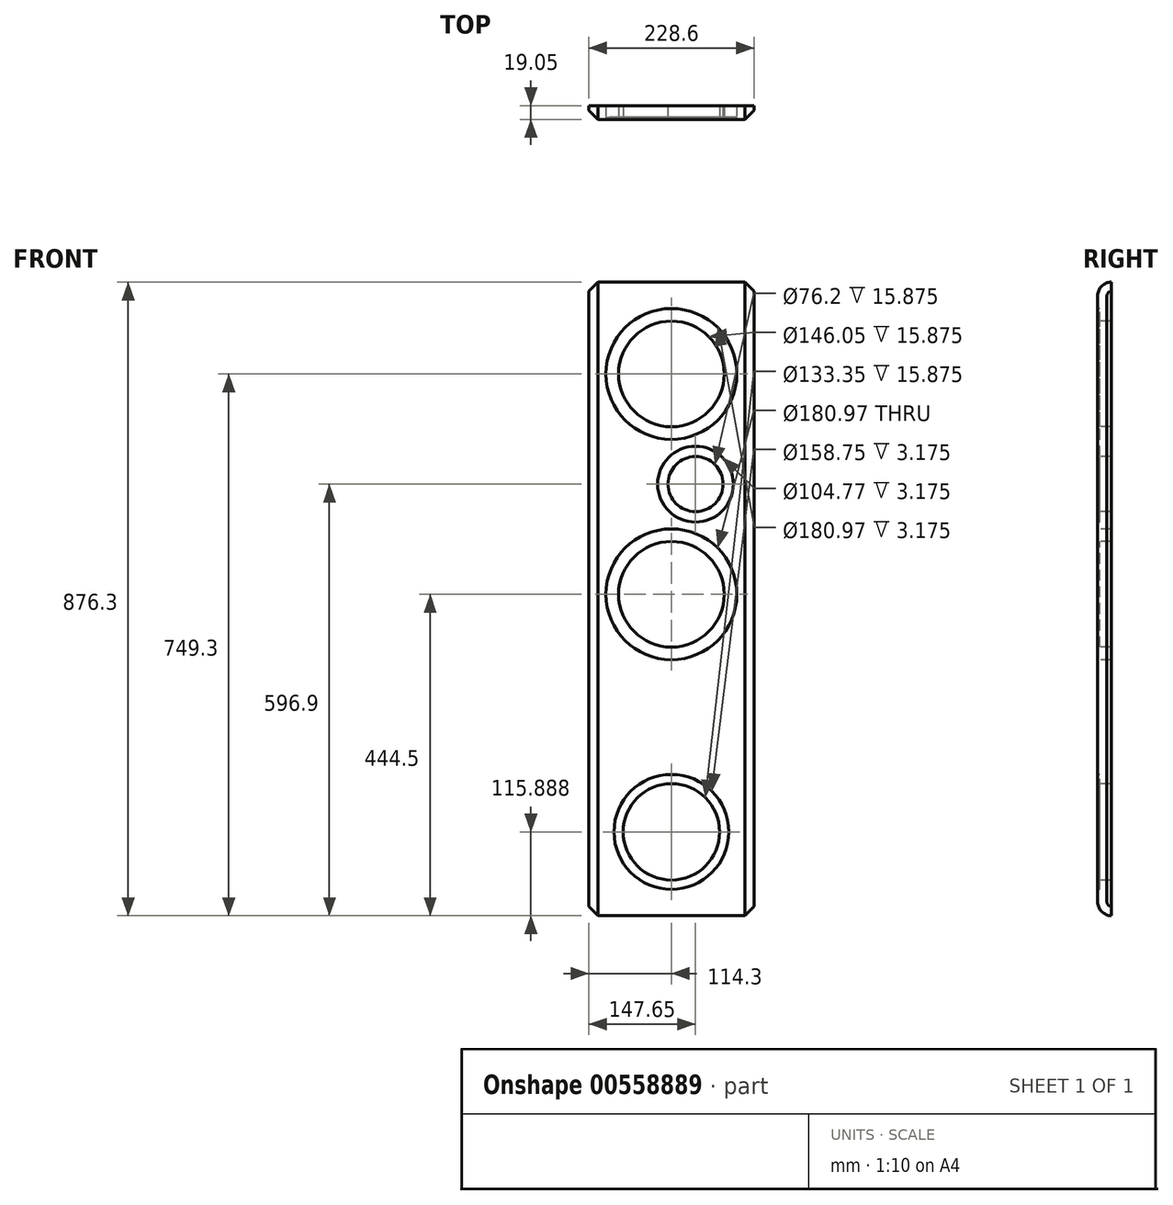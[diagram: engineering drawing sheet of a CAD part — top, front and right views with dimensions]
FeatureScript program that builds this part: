
annotation { "Feature Type Name" : "Feature", "Feature Type Description" : "" }
export const myFeature = defineFeature(function(context is Context, id is Id, definition is map)
    precondition{}
    {
        {
            var Q0;
            Q0=qCreatedBy(makeId("Front.planeOp"),FACE);
            var sketch = newSketch(context, id + "F0", { "sketchPlane" : qUnion([Q0])});
            skLineSegment(sketch, "E0.bottom", {"start": v(-114.3, 914.4) * mm, "end": v(114.3, 914.4) * mm});
            skLineSegment(sketch, "E0.top", {"start": v(-114.3, 38.1) * mm, "end": v(114.3, 38.1) * mm});
            skLineSegment(sketch, "E0.left", {"start": v(-114.3, 914.4) * mm, "end": v(-114.3, 38.1) * mm});
            skLineSegment(sketch, "E0.right", {"start": v(114.3, 914.4) * mm, "end": v(114.3, 38.1) * mm});
            skCircle(sketch, "E1", {"center": v(0, 787.4) * mm, "radius": 90.49 * mm});
            skCircle(sketch, "E2", {"center": v(33.35, 635) * mm, "radius": 38.1 * mm});
            skCircle(sketch, "E3", {"center": v(0, 787.4) * mm, "radius": 73.03 * mm});
            skCircle(sketch, "E4", {"center": v(33.35, 635) * mm, "radius": 52.39 * mm});
            skLineSegment(sketch, "E5", {"start": v(307.03, 635) * mm, "end": v(439.89, 635) * mm});
            skCircle(sketch, "E6.MirrorC", {"center": v(0, 482.6) * mm, "radius": 73.03 * mm});
            skCircle(sketch, "E7.MirrorC", {"center": v(0, 482.6) * mm, "radius": 90.49 * mm});
            skLineSegment(sketch, "E8", {"start": v(299.18, 355.6) * mm, "end": v(426.8, 355.6) * mm});
            skCircle(sketch, "E9", {"center": v(0, 153.99) * mm, "radius": 79.38 * mm});
            skLineSegment(sketch, "E10", {"start": v(333.82, 877.89) * mm, "end": v(430.62, 877.89) * mm});
            skLineSegment(sketch, "E11", {"start": v(409.67, 74.61) * mm, "end": v(278.97, 74.61) * mm});
            skLineSegment(sketch, "E12", {"start": v(430.62, 877.89) * mm, "end": v(430.62, 914.4) * mm});
            skLineSegment(sketch, "E13", {"start": v(409.67, 74.61) * mm, "end": v(409.67, 38.1) * mm});
            skCircle(sketch, "E14", {"center": v(0, 153.99) * mm, "radius": 66.68 * mm});
            skLineSegment(sketch, "E15", {"start": v(323.31, 692.15) * mm, "end": v(428.61, 692.15) * mm});
            skLineSegment(sketch, "E16", {"start": v(428.61, 687.39) * mm, "end": v(321.83, 687.39) * mm});
            skLineSegment(sketch, "E17", {"start": v(321.83, 696.91) * mm, "end": v(434.54, 696.91) * mm});
            skLineSegment(sketch, "E18", {"start": v(307.98, 392.11) * mm, "end": v(424.03, 392.11) * mm});
            skSolve(sketch);
        }
        {
            var Q0;
            Q0=makeQuery(id+"F0.imprint","IMPRINT",FACE,{"disambiguationData":[TD([[makeQuery(id+"F0.imprint","IMPRINT",EDGE,{"derivedFrom":sQuery(id+"F0.wireOp",EDGE,"E0.bottom")}),-1.0]])]});
            var Q1;
            Q1=makeQuery(id+"F0.imprint","IMPRINT",FACE,{"disambiguationData":[TD([[makeQuery(id+"F0.imprint","IMPRINT",EDGE,{"derivedFrom":sQuery(id+"F0.wireOp",EDGE,"E1")}),1.0]])]});
            var Q2;
            Q2=makeQuery(id+"F0.imprint","IMPRINT",FACE,{"disambiguationData":[TD([[makeQuery(id+"F0.imprint","IMPRINT",EDGE,{"derivedFrom":sQuery(id+"F0.wireOp",EDGE,"E2")}),-1.0]])]});
            var Q3;
            Q3=makeQuery(id+"F0.imprint","IMPRINT",FACE,{"disambiguationData":[TD([[makeQuery(id+"F0.imprint","IMPRINT",EDGE,{"derivedFrom":sQuery(id+"F0.wireOp",EDGE,"E6.MirrorC")}),1.0]])]});
            var Q4;
            Q4=makeQuery(id+"F0.imprint","IMPRINT",FACE,{"disambiguationData":[TD([[makeQuery(id+"F0.imprint","IMPRINT",EDGE,{"derivedFrom":sQuery(id+"F0.wireOp",EDGE,"E9")}),1.0]])]});
            extrude(context, id + "F1", {"entities" : qUnion([Q0, Q1, Q2, Q3, Q4]), "oppositeDirection" : true, "depth" : 19.05 * mm});
        }
        {
            var Q0;
            Q0=makeQuery(id+"F0.imprint","IMPRINT",FACE,{"disambiguationData":[TD([[makeQuery(id+"F0.imprint","IMPRINT",EDGE,{"derivedFrom":sQuery(id+"F0.wireOp",EDGE,"E1")}),1.0]])]});
            var Q1;
            Q1=makeQuery(id+"F0.imprint","IMPRINT",FACE,{"disambiguationData":[TD([[makeQuery(id+"F0.imprint","IMPRINT",EDGE,{"derivedFrom":sQuery(id+"F0.wireOp",EDGE,"E2")}),-1.0]])]});
            var Q2;
            Q2=makeQuery(id+"F0.imprint","IMPRINT",FACE,{"disambiguationData":[TD([[makeQuery(id+"F0.imprint","IMPRINT",EDGE,{"derivedFrom":sQuery(id+"F0.wireOp",EDGE,"E6.MirrorC")}),1.0]])]});
            var Q3;
            Q3=makeQuery(id+"F0.imprint","IMPRINT",FACE,{"disambiguationData":[TD([[makeQuery(id+"F0.imprint","IMPRINT",EDGE,{"derivedFrom":sQuery(id+"F0.wireOp",EDGE,"E9")}),1.0]])]});
            extrude(context, id + "F2", {"entities" : qUnion([Q0, Q1, Q2, Q3]), "operationType" : NewBodyOperationType.REMOVE, "oppositeDirection" : true, "depth" : 3.17 * mm});
        }
        {
            var Q0;
            Q0=qCreatedBy(makeId("Top.planeOp"),FACE);
            var sketch = newSketch(context, id + "F3", { "sketchPlane" : qUnion([Q0])});
            skLineSegment(sketch, "E19.bottom", {"start": v(-114.3, 0) * mm, "end": v(114.3, 0) * mm});
            skLineSegment(sketch, "E19.top", {"start": v(-114.3, 508) * mm, "end": v(114.3, 508) * mm});
            skLineSegment(sketch, "E19.left", {"start": v(-114.3, 0) * mm, "end": v(-114.3, 508) * mm});
            skLineSegment(sketch, "E19.right", {"start": v(114.3, 0) * mm, "end": v(114.3, 508) * mm});
            skSolve(sketch);
        }
        {
            var Q0;
            Q0=makeQuery(id+"F1.opExtrude","CAP_EDGE",EDGE,{"disambiguationData":[OSD([sQuery(id+"F0.wireOp",EDGE,"E0.bottom")])],"isStart":true});
            var Q1;
            Q1=makeQuery(id+"F1.opExtrude","CAP_EDGE",EDGE,{"disambiguationData":[OSD([sQuery(id+"F0.wireOp",EDGE,"E0.top")])],"isStart":true});
            fillet(context, id + "F4", {"entities" : qUnion([Q0, Q1]), "radius" : 19.05 * mm, "tangentPropagation" : true, "allowEdgeOverflow" : false});
        }
        {
            var Q0;
            Q0=makeQuery(id+"F1.opExtrude","CAP_EDGE",EDGE,{"disambiguationData":[OSD([sQuery(id+"F0.wireOp",EDGE,"E0.left")])],"isStart":true});
            var Q1;
            Q1=makeQuery(id+"F1.opExtrude","CAP_EDGE",EDGE,{"disambiguationData":[OSD([sQuery(id+"F0.wireOp",EDGE,"E0.right")])],"isStart":true});
            chamfer(context, id + "F5", {"entities" : qUnion([Q0, Q1]), "width" : 12.7 * mm, "tangentPropagation" : true});
        }
    });
